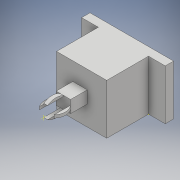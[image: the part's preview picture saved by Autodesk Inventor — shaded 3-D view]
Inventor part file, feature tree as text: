
AUTODESK INVENTOR PART (.ipt)
format: ipt  version: 2018 (Build 220112000, 112)  size: 176,640 bytes
history: native  units: mm
features: sketch x12, extrude x7
ambient origin geometry x8: Origin, YZ Plane, XZ Plane, XY Plane, X Axis, Y Axis, Z Axis, Center Point
bodies: Solid1 (feature_tree)
feature tree (19):
  extrude  "Extrusion1"  Depth=10.0mm
  sketch  "Sketch2"  dims[d2=60.0mm d3=50.0mm]
  extrude  "Extrusion2"  Depth=50.0mm
  extrude  "Extrusion3"  Depth=20.0mm TaperAngle=0.0deg
  sketch  "Sketch5"  dims[d13=20.0mm d14=0.0mm d15=20.0mm d16=0.0mm]
  sketch  "Sketch6"  dims[d17=20.0mm d18=0.0mm]
  sketch  "Sketch7"
  sketch  "Sketch8"
  extrude  "Extrusion4"  Depth=20.0mm TaperAngle=0.0deg
  extrude  "Extrusion5"  Depth=20.0mm TaperAngle=0.0deg
  extrude  "Extrusion6"  [1 undecoded]
  extrude  "Extrusion7"  [1 undecoded]
  sketch  "Sketch1"  dims[d0=100.0mm d1=10.0mm]
  sketch  "Sketch3"  dims[d4=60.0mm d5=0.0mm d6=20.0mm d7=0.0mm]
  sketch  "Sketch4"  dims[d8=20.0mm d9=0.0mm d11=20.0mm d12=0.0mm]
  sketch  "Sketch9"
  sketch  "Sketch10"
  sketch  "Sketch11"
  sketch  "Sketch12"
note: 2 required parameter values undecoded (feature->parameter linkage not recoverable at this tier; creation-order binding heuristic only, values carry confidence <= 0.55)
